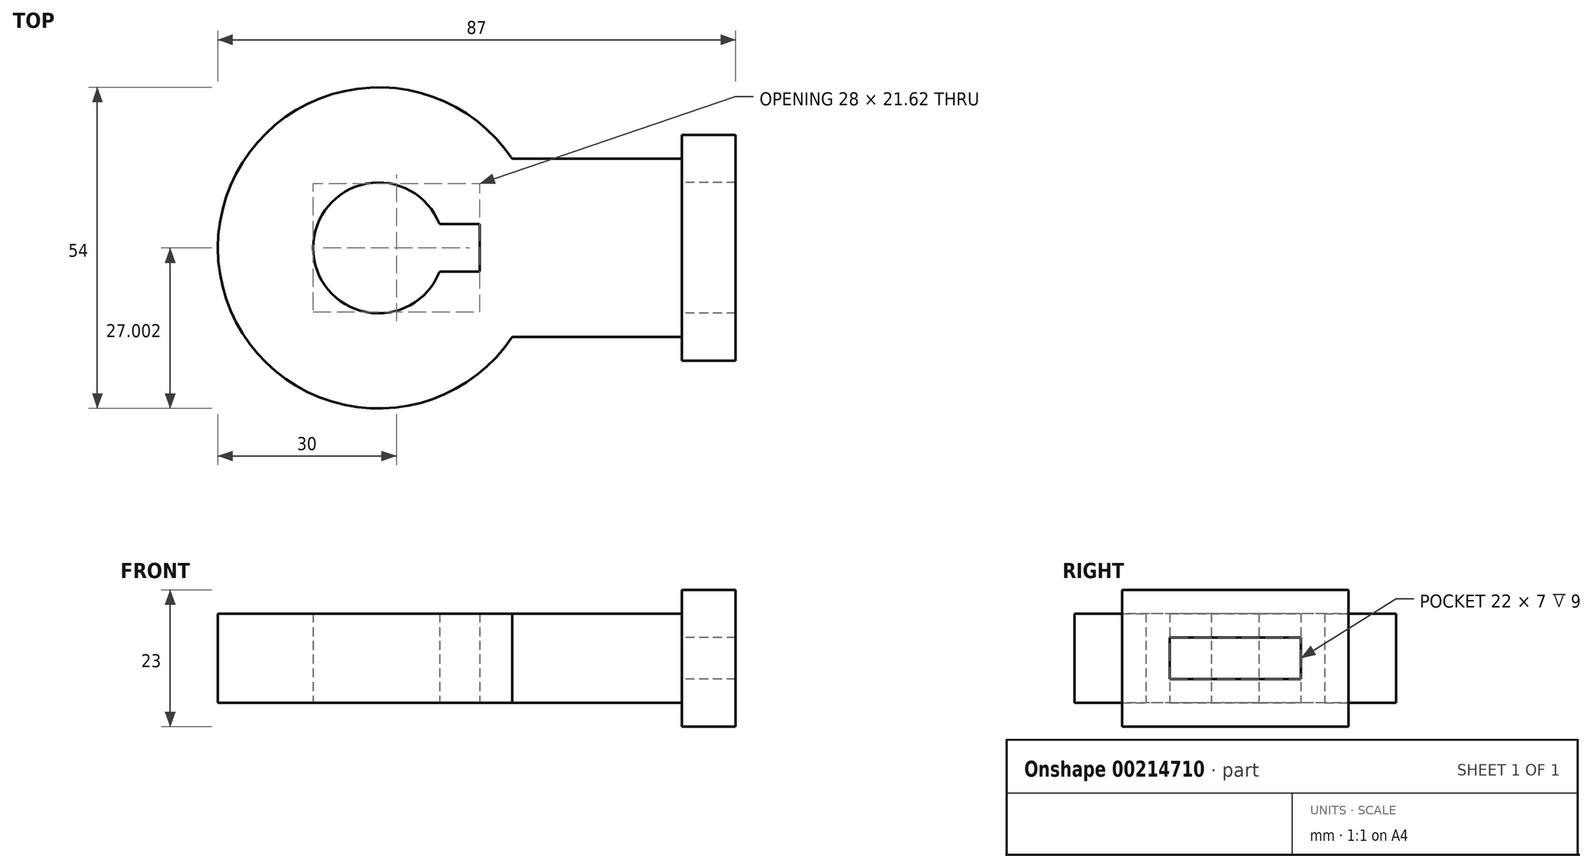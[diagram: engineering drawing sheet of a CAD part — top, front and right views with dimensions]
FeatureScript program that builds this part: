
annotation { "Feature Type Name" : "Feature", "Feature Type Description" : "" }
export const myFeature = defineFeature(function(context is Context, id is Id, definition is map)
    precondition{}
    {
        {
            var Q0;
            Q0=qCreatedBy(makeId("Top.planeOp"),FACE);
            var sketch = newSketch(context, id + "F0", { "sketchPlane" : qUnion([Q0])});
            skArc(sketch, "E0", {"start": v(-42.48, 30.58) * mm, "mid": v(-63.73, 26.58) * mm, "end": v(-42.48, 22.58) * mm});
            skLineSegment(sketch, "E1", {"start": v(-1.73, 26.58) * mm, "end": v(-1.73, 11.58) * mm});
            skLineSegment(sketch, "E2", {"start": v(-1.73, 26.58) * mm, "end": v(-1.73, 41.58) * mm});
            skLineSegment(sketch, "E3", {"start": v(-1.73, 41.58) * mm, "end": v(-30.28, 41.58) * mm});
            skLineSegment(sketch, "E4", {"start": v(-1.73, 11.58) * mm, "end": v(-30.28, 11.58) * mm});
            skArc(sketch, "E5", {"start": v(-30.28, 11.58) * mm, "mid": v(-79.73, 26.58) * mm, "end": v(-30.28, 41.58) * mm});
            skLineSegment(sketch, "E6", {"start": v(-35.73, 26.58) * mm, "end": v(-35.73, 30.58) * mm});
            skLineSegment(sketch, "E7", {"start": v(-35.73, 30.58) * mm, "end": v(-42.48, 30.58) * mm});
            skLineSegment(sketch, "E8", {"start": v(-35.73, 26.58) * mm, "end": v(-35.73, 22.58) * mm});
            skLineSegment(sketch, "E9", {"start": v(-35.73, 22.58) * mm, "end": v(-42.48, 22.58) * mm});
            skSolve(sketch);
        }
        {
            var Q0;
            Q0=makeQuery(id+"F0.imprint","IMPRINT",FACE,{"disambiguationData":[TD([[makeQuery(id+"F0.imprint","IMPRINT",EDGE,{"derivedFrom":sQuery(id+"F0.wireOp",EDGE,"E0")}),-1.0]])]});
            extrude(context, id + "F1", {"entities" : qUnion([Q0]), "depth" : 15 * mm});
        }
        {
            var Q0;
            Q0=makeQuery(id+"F1.opExtrude","SWEPT_FACE",FACE,{"disambiguationData":[OSD([sQuery(id+"F0.wireOp",EDGE,"E1"),sQuery(id+"F0.wireOp",EDGE,"E2")])]});
            var sketch = newSketch(context, id + "F2", { "sketchPlane" : qUnion([Q0])});
            skPoint(sketch, "E10.endSnap0", {"position": v(11.58, 7.5) * mm});
            skLineSegment(sketch, "E11", {"start": v(26.58, 11) * mm, "end": v(37.58, 11) * mm});
            skLineSegment(sketch, "E12", {"start": v(15.58, 11) * mm, "end": v(26.58, 11) * mm});
            skPoint(sketch, "E13.orphan", {"position": v(26.58, 0) * mm});
            skPoint(sketch, "E10.end.orphan", {"position": v(26.58, 7.5) * mm});
            skLineSegment(sketch, "E14", {"start": v(37.58, 11) * mm, "end": v(37.58, 4) * mm});
            skLineSegment(sketch, "E15", {"start": v(37.58, 4) * mm, "end": v(15.58, 4) * mm});
            skLineSegment(sketch, "E16", {"start": v(15.58, 4) * mm, "end": v(15.58, 11) * mm});
            skPoint(sketch, "E17.endSnap0", {"position": v(26.58, 15) * mm});
            skLineSegment(sketch, "E18", {"start": v(26.58, 19) * mm, "end": v(45.58, 19) * mm});
            skLineSegment(sketch, "E19", {"start": v(45.58, 19) * mm, "end": v(45.58, -4) * mm});
            skLineSegment(sketch, "E20", {"start": v(45.58, -4) * mm, "end": v(7.58, -4) * mm});
            skLineSegment(sketch, "E21", {"start": v(7.58, -4) * mm, "end": v(7.58, 19) * mm});
            skLineSegment(sketch, "E22", {"start": v(7.58, 19) * mm, "end": v(26.58, 19) * mm});
            skSolve(sketch);
        }
        {
            var Q0;
            Q0=makeQuery(id+"F2.imprint","IMPRINT",FACE,{"disambiguationData":[TD([[makeQuery(id+"F2.imprint","IMPRINT",EDGE,{"derivedFrom":sQuery(id+"F2.wireOp",EDGE,"E11")}),1.0]])]});
            var Q1;
            Q1=makeQuery(id+"F2.imprint","IMPRINT",FACE,{"disambiguationData":[TD([[makeQuery(id+"F2.imprint","IMPRINT",EDGE,{"derivedFrom":sQuery(id+"F2.wireOp",EDGE,"E18")}),-1.0]])]});
            extrude(context, id + "F3", {"entities" : qUnion([Q0, Q1]), "operationType" : NewBodyOperationType.ADD, "depth" : 9 * mm});
        }
    });
